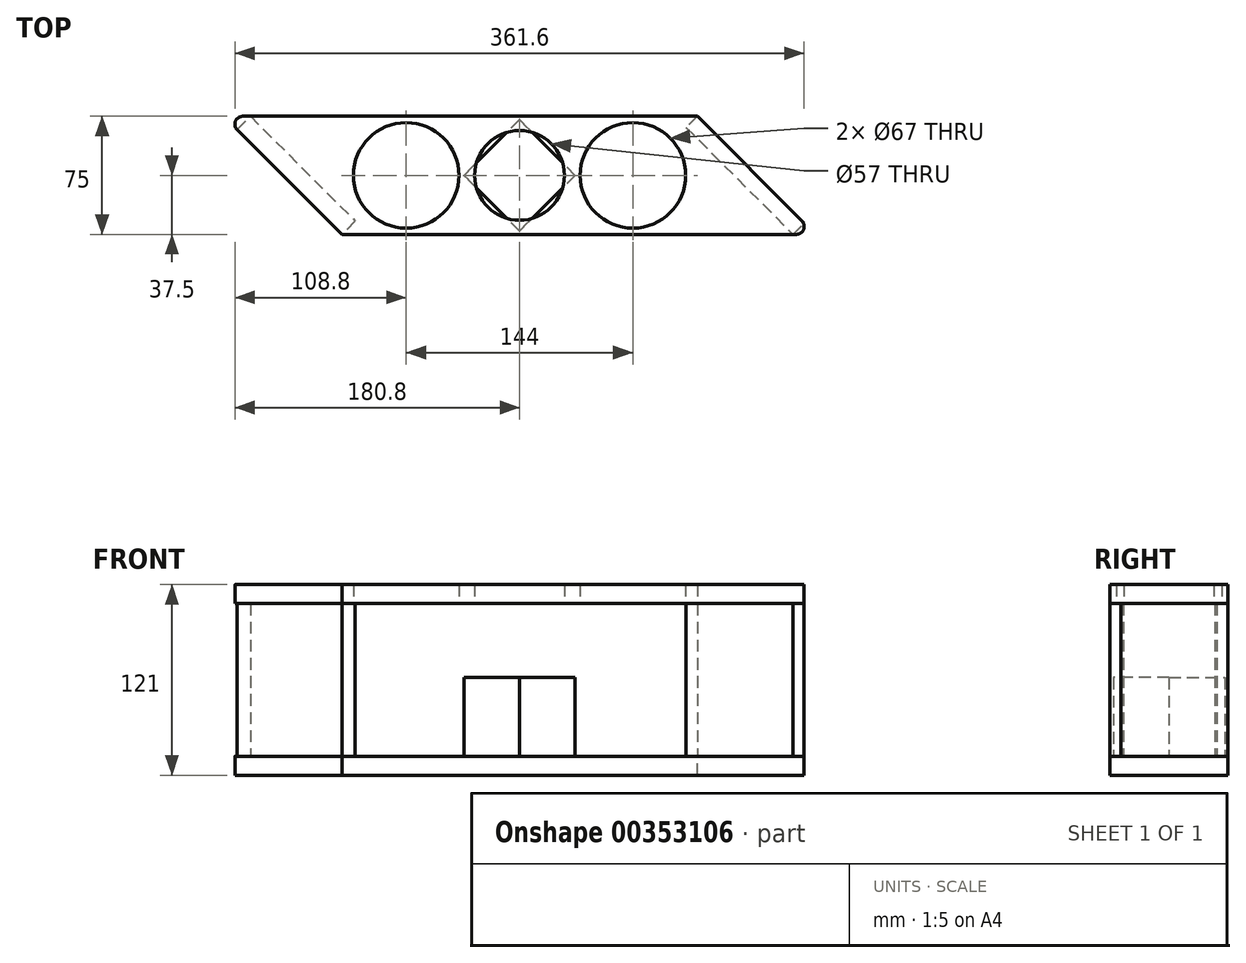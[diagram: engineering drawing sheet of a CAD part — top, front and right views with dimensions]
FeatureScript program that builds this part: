
annotation { "Feature Type Name" : "Feature", "Feature Type Description" : "" }
export const myFeature = defineFeature(function(context is Context, id is Id, definition is map)
    precondition{}
    {
        {
            var Q0;
            Q0=qCreatedBy(makeId("Top.planeOp"),FACE);
            var sketch = newSketch(context, id + "F0", { "sketchPlane" : qUnion([Q0])});
            skLineSegment(sketch, "E0.bottom", {"start": v(187.87, -37.5) * mm, "end": v(-112.87, -37.5) * mm});
            skLineSegment(sketch, "E0.top", {"start": v(112.87, 37.5) * mm, "end": v(-187.87, 37.5) * mm});
            skLineSegment(sketch, "E0.left", {"start": v(187.87, -37.5) * mm, "end": v(112.87, 37.5) * mm});
            skLineSegment(sketch, "E0.right", {"start": v(-112.87, -37.5) * mm, "end": v(-187.87, 37.5) * mm});
            skPoint(sketch, "E0.middle", {"position": v(0, 0) * mm});
            skLineSegment(sketch, "E1", {"start": v(-150.37, 0) * mm, "end": v(150.37, 0) * mm, "construction": true});
            skCircle(sketch, "E2", {"center": v(72, 0) * mm, "radius": 33.5 * mm});
            skCircle(sketch, "E3", {"center": v(0, 0) * mm, "radius": 28.5 * mm});
            skLineSegment(sketch, "E4", {"start": v(0, 37.5) * mm, "end": v(0, -37.5) * mm, "construction": true});
            skCircle(sketch, "E5.MirrorC", {"center": v(-72, 0) * mm, "radius": 33.5 * mm});
            skLineSegment(sketch, "E6", {"start": v(-179.38, 29.01) * mm, "end": v(-170.9, 37.5) * mm});
            skLineSegment(sketch, "E7", {"start": v(-170.9, 37.5) * mm, "end": v(-104.38, -29.01) * mm});
            skLineSegment(sketch, "E8", {"start": v(-104.38, -29.01) * mm, "end": v(-112.87, -37.5) * mm});
            skLineSegment(sketch, "E9", {"start": v(-104.38, -29.01) * mm, "end": v(-97.31, -21.94) * mm, "construction": true});
            skLineSegment(sketch, "E10", {"start": v(-38.5, 0) * mm, "end": v(-28.5, 0) * mm, "construction": true});
            skLineSegment(sketch, "E11", {"start": v(112.87, 37.5) * mm, "end": v(105.8, 30.43) * mm});
            skLineSegment(sketch, "E12", {"start": v(105.8, 30.43) * mm, "end": v(173.73, -37.5) * mm});
            skLineSegment(sketch, "E13", {"start": v(173.73, -37.5) * mm, "end": v(180.8, -30.43) * mm});
            skSolve(sketch);
        }
        {
            var Q0;
            Q0=qCreatedBy(makeId("Top.planeOp"),FACE);
            cPlane(context, id + "F1", {"entities" : qUnion([Q0]), "cplaneType" : CPlaneType.OFFSET, "offset" : 97 * mm, "width" : 150 * mm, "height" : 150 * mm});
        }
        {
            var Q0;
            Q0=qCreatedBy(makeId("Top.planeOp"),FACE);
            var sketch = newSketch(context, id + "F2", { "sketchPlane" : qUnion([Q0])});
            skLineSegment(sketch, "E14.0", {"start": v(112.87, 37.5) * mm, "end": v(-187.87, 37.5) * mm});
            skLineSegment(sketch, "E14.1", {"start": v(-112.87, -37.5) * mm, "end": v(-187.87, 37.5) * mm});
            skLineSegment(sketch, "E14.2", {"start": v(187.87, -37.5) * mm, "end": v(-112.87, -37.5) * mm});
            skPoint(sketch, "E14.3", {"position": v(187.87, -37.5) * mm});
            skLineSegment(sketch, "E14.4", {"start": v(187.87, -37.5) * mm, "end": v(112.87, 37.5) * mm});
            skSolve(sketch);
        }
        {
            var Q0;
            Q0 = qSketchRegion(id + "F2", true);
            extrude(context, id + "F3", {"entities" : qUnion([Q0]), "oppositeDirection" : true, "depth" : 12 * mm});
        }
        {
            var Q0;
            Q0=qCreatedBy(id+"F1.planeOp",FACE);
            var sketch = newSketch(context, id + "F4", { "sketchPlane" : qUnion([Q0])});
            skLineSegment(sketch, "E15.0", {"start": v(112.87, 37.5) * mm, "end": v(-187.87, 37.5) * mm});
            skLineSegment(sketch, "E15.1", {"start": v(-112.87, -37.5) * mm, "end": v(-187.87, 37.5) * mm});
            skLineSegment(sketch, "E15.2", {"start": v(187.87, -37.5) * mm, "end": v(-112.87, -37.5) * mm});
            skPoint(sketch, "E15.3", {"position": v(187.87, -37.5) * mm});
            skLineSegment(sketch, "E15.4", {"start": v(187.87, -37.5) * mm, "end": v(112.87, 37.5) * mm});
            skCircle(sketch, "E16.0", {"center": v(-72, 0) * mm, "radius": 33.5 * mm});
            skCircle(sketch, "E16.1", {"center": v(0, 0) * mm, "radius": 28.5 * mm});
            skCircle(sketch, "E16.2", {"center": v(72, 0) * mm, "radius": 33.5 * mm});
            skSolve(sketch);
        }
        {
            var Q0;
            Q0 = qSketchRegion(id + "F4", true);
            extrude(context, id + "F5", {"entities" : qUnion([Q0]), "depth" : 12 * mm});
        }
        {
            var Q0;
            {var subQ2=sQuery(id+"F0.wireOp",EDGE,"E6");Q0=makeQuery(id+"F0.imprint","IMPRINT",FACE,{"disambiguationData":[TD([[makeQuery(id+"F0.imprint","IMPRINT",EDGE,{"derivedFrom":subQ2}),-1.0]])]});}
            var Q1;
            {var subQ0=sQuery(id+"F0.wireOp",EDGE,"E11");Q1=makeQuery(id+"F0.imprint","IMPRINT",FACE,{"disambiguationData":[TD([[makeQuery(id+"F0.imprint","IMPRINT",EDGE,{"derivedFrom":subQ0}),1.0]])]});}
            var Q2;
            Q2=makeQuery(id+"F5.opExtrude","CAP_FACE",FACE,{"disambiguationData":[OSD([sQuery(id+"F4.wireOp",EDGE,"E15.0"),sQuery(id+"F4.wireOp",EDGE,"E15.1"),sQuery(id+"F4.wireOp",EDGE,"E15.2"),sQuery(id+"F4.wireOp",EDGE,"E15.4"),sQuery(id+"F4.wireOp",EDGE,"E16.0"),sQuery(id+"F4.wireOp",EDGE,"E16.1"),sQuery(id+"F4.wireOp",EDGE,"E16.2")])],"isStart":true});
            extrude(context, id + "F6", {"entities" : qUnion([Q0, Q1]), "endBound" : BoundingType.UP_TO_SURFACE, "endBoundEntityFace" : qUnion([Q2]), "depth" : 25 * mm});
        }
        {
            var Q0;
            Q0=makeQuery(id+"F3.opExtrude","CAP_FACE",FACE,{"disambiguationData":[OSD([sQuery(id+"F2.wireOp",EDGE,"E14.0"),sQuery(id+"F2.wireOp",EDGE,"E14.1"),sQuery(id+"F2.wireOp",EDGE,"E14.2"),sQuery(id+"F2.wireOp",EDGE,"E14.4")])],"isStart":true});
            var sketch = newSketch(context, id + "F7", { "sketchPlane" : qUnion([Q0])});
            skLineSegment(sketch, "E17.bottom", {"start": v(35.36, 0) * mm, "end": v(0, -35.36) * mm});
            skLineSegment(sketch, "E17.top", {"start": v(0, 35.36) * mm, "end": v(-35.36, 0) * mm});
            skLineSegment(sketch, "E17.left", {"start": v(35.36, 0) * mm, "end": v(0, 35.36) * mm});
            skLineSegment(sketch, "E17.right", {"start": v(0, -35.36) * mm, "end": v(-35.36, 0) * mm});
            skPoint(sketch, "E17.middle", {"position": v(0, 0) * mm});
            skSolve(sketch);
        }
        {
            var Q0;
            Q0 = qSketchRegion(id + "F7", true);
            extrude(context, id + "F8", {"entities" : qUnion([Q0]), "operationType" : NewBodyOperationType.ADD, "depth" : 50 * mm});
        }
        {
            var Q0;
            Q0=makeQuery(id+"F5.opExtrude","SWEPT_EDGE",EDGE,{"disambiguationData":[OSD([sQuery(id+"F4.wireOp",EDGE,"E15.0"),sQuery(id+"F4.wireOp",EDGE,"E15.1")])]});
            var Q1;
            Q1=makeQuery(id+"F3.opExtrude","SWEPT_EDGE",EDGE,{"disambiguationData":[OSD([sQuery(id+"F2.wireOp",EDGE,"E14.0"),sQuery(id+"F2.wireOp",EDGE,"E14.1")])]});
            var Q2;
            Q2=makeQuery(id+"F5.opExtrude","SWEPT_EDGE",EDGE,{"disambiguationData":[OSD([sQuery(id+"F4.wireOp",EDGE,"E15.2"),sQuery(id+"F4.wireOp",EDGE,"E15.4")])]});
            var Q3;
            Q3=makeQuery(id+"F3.opExtrude","SWEPT_EDGE",EDGE,{"disambiguationData":[OSD([sQuery(id+"F2.wireOp",EDGE,"E14.2"),sQuery(id+"F2.wireOp",EDGE,"E14.4")])]});
            fillet(context, id + "F9", {"entities" : qUnion([Q0, Q1, Q2, Q3]), "radius" : 5 * mm, "tangentPropagation" : true, "allowEdgeOverflow" : false});
        }
    });
